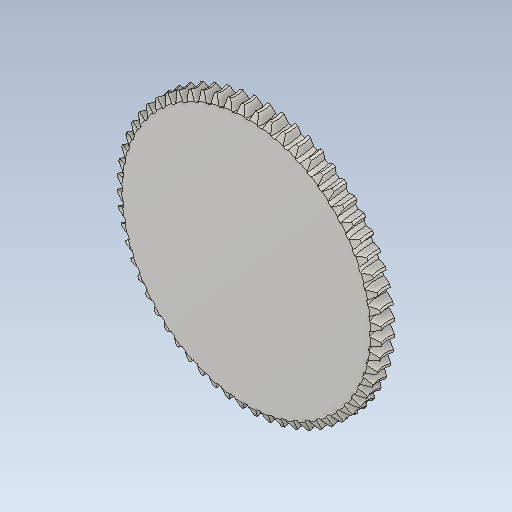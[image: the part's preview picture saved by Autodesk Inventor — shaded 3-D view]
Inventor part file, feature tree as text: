
AUTODESK INVENTOR PART (.ipt)
format: ipt  version: 2021.1 (Build 251245010, 245A)  size: 876,544 bytes
history: native  units: mm (DEFAULTED — no unit token found)
features: other x8, plane x3, pattern_circular x1, sketch x1
ambient origin geometry x5: Origin, X Axis, Y Axis, Z Axis, Center Point
bodies: Solid1 (feature_tree)
feature tree (13):
  other  "Tooth Plane"
  other  "Base Body Sketch"
  other  "Base Body"
  other  "Base Body2"
  plane  "Work Plane13"
  other  "Tooth"
  pattern_circular  "Tooth Pattern"  [2 undecoded]
  plane  "Work Plane14"
  plane  "Work Plane15"
  other  "Tooth Sketch"
  sketch  "Sketch8"  dims[d35=90.0deg d37=-0.996687mm d38=48.106173mm d39=3.490659mm d40=5.222956mm d41=6.87231mm d42=1.2954mm d43=90.0deg d44=600.0mm d46=360.0deg d50=3.952068mm d68=48.106173mm d69=0.0mm d73=0.0mm d75=0.523599mm d77=82.467725mm d78=6.35mm d79=0.0mm d80=0.0mm d81=0.0mm d82=0.0mm d83=0.523599mm d84=0.0mm d85=180.0deg d86=48.106173mm d87=86.591112mm d89=10.995697mm d90=90.0deg d92=6.35mm d93=48.106173mm]
  other  "Srf1"
  other  "Pitch Diameter"
note: 2 required parameter values undecoded (feature->parameter linkage not recoverable at this tier; creation-order binding heuristic only, values carry confidence <= 0.55)
